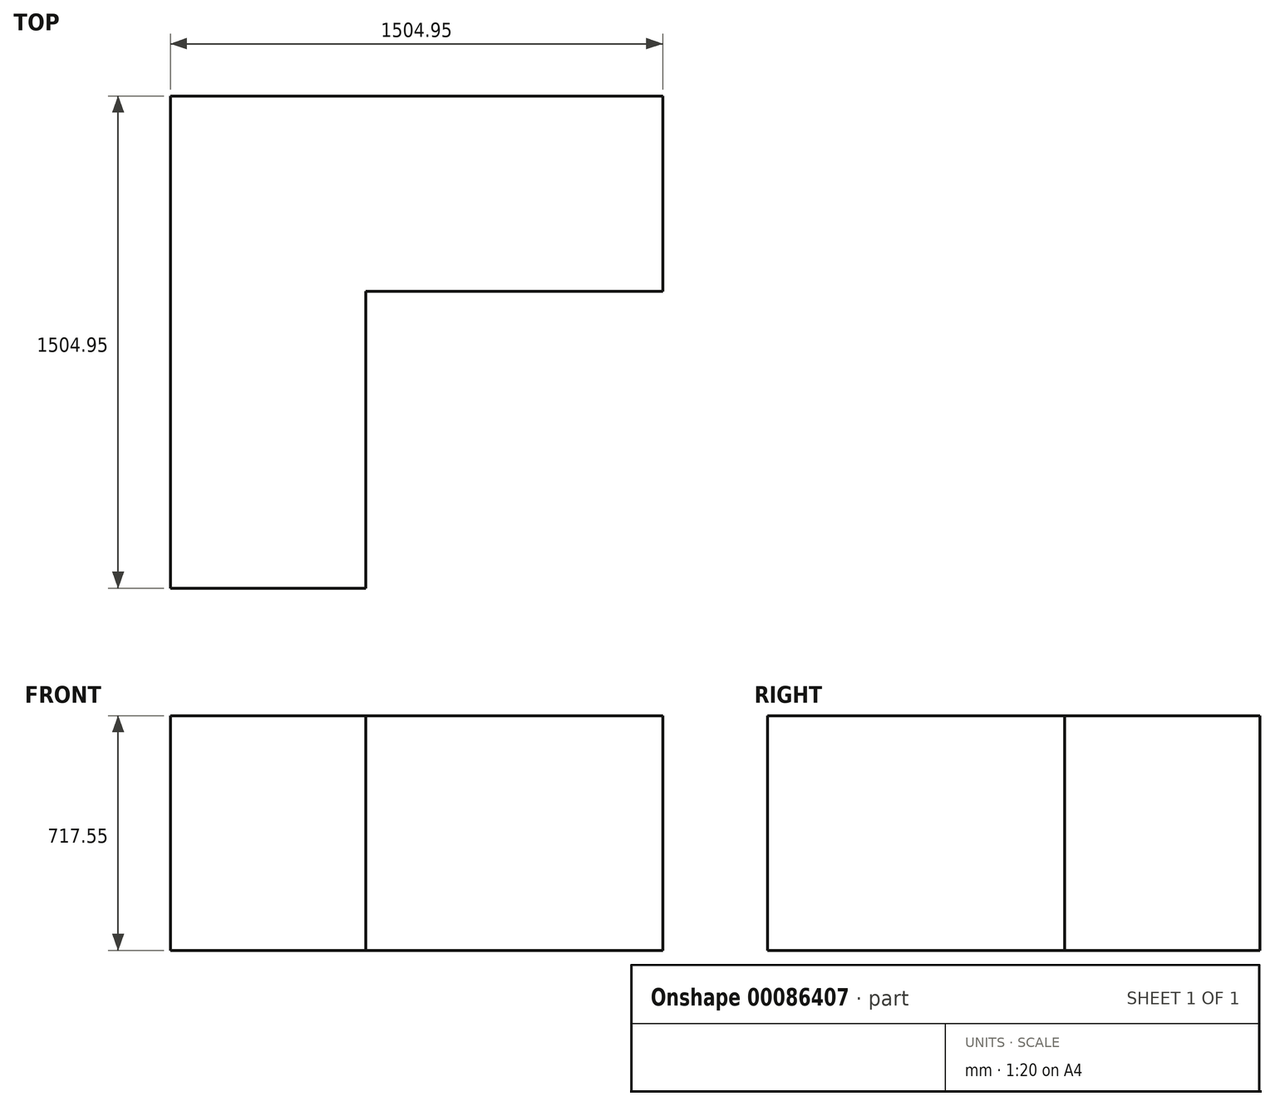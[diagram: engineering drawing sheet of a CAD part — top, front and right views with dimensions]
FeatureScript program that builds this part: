
annotation { "Feature Type Name" : "Feature", "Feature Type Description" : "" }
export const myFeature = defineFeature(function(context is Context, id is Id, definition is map)
    precondition{}
    {
        {
            var Q0;
            Q0=qCreatedBy(makeId("Top.planeOp"),FACE);
            var sketch = newSketch(context, id + "F0", { "sketchPlane" : qUnion([Q0])});
            skLineSegment(sketch, "E0", {"start": v(897.6, 607.88) * mm, "end": v(-607.35, 607.88) * mm});
            skLineSegment(sketch, "E1", {"start": v(-607.35, 607.88) * mm, "end": v(-607.35, -897.07) * mm});
            skLineSegment(sketch, "E2", {"start": v(-607.35, -897.07) * mm, "end": v(-10.45, -897.07) * mm});
            skLineSegment(sketch, "E3", {"start": v(-10.45, -897.07) * mm, "end": v(-10.45, 10.98) * mm});
            skLineSegment(sketch, "E4", {"start": v(-10.45, 10.98) * mm, "end": v(897.6, 10.98) * mm});
            skLineSegment(sketch, "E5", {"start": v(897.6, 10.98) * mm, "end": v(897.6, 607.88) * mm});
            skSolve(sketch);
        }
        {
            var Q0;
            Q0 = qSketchRegion(id + "F0", true);
            extrude(context, id + "F1", {"entities" : qUnion([Q0]), "depth" : 717.55 * mm});
        }
    });
